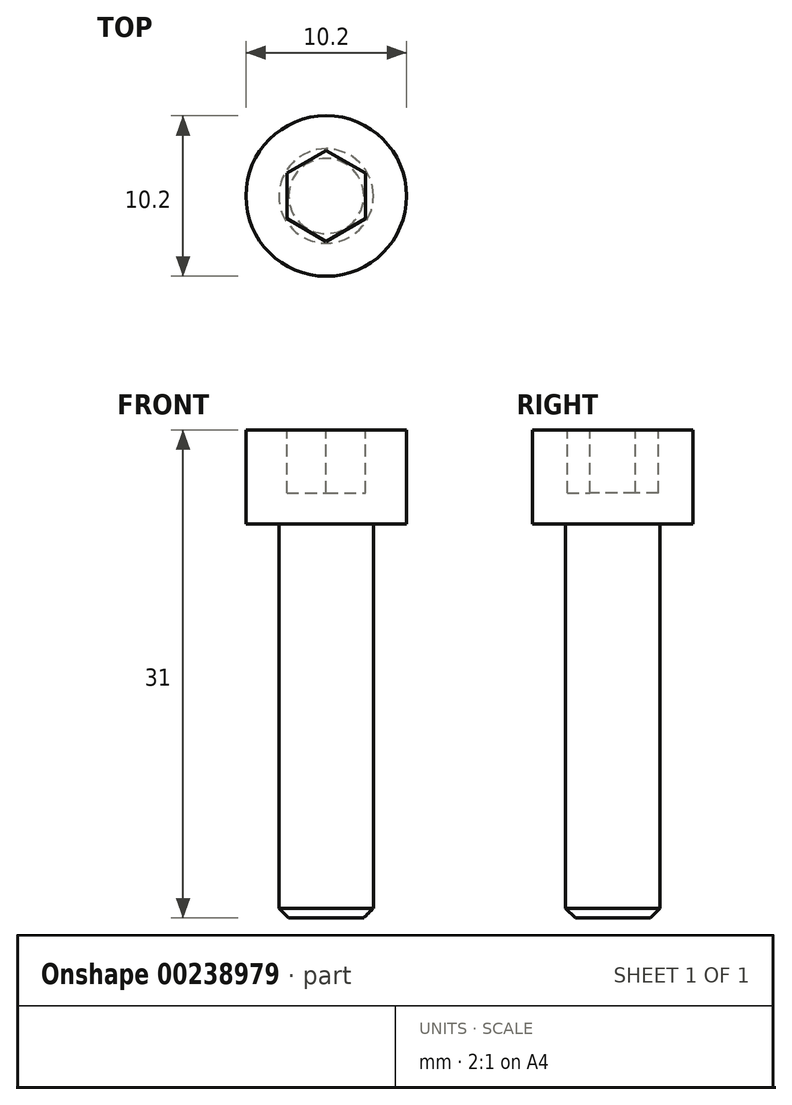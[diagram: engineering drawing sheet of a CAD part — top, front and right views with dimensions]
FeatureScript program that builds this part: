
annotation { "Feature Type Name" : "Feature", "Feature Type Description" : "" }
export const myFeature = defineFeature(function(context is Context, id is Id, definition is map)
    precondition{}
    {
        {
            var Q0;
            Q0=qCreatedBy(makeId("Front.planeOp"),FACE);
            var sketch = newSketch(context, id + "F0", { "sketchPlane" : qUnion([Q0])});
            skLineSegment(sketch, "E0", {"start": v(-5.1, 6) * mm, "end": v(-5.1, 0) * mm});
            skLineSegment(sketch, "E1", {"start": v(-5.1, 6) * mm, "end": v(0, 6) * mm});
            skLineSegment(sketch, "E2", {"start": v(-3, 0) * mm, "end": v(-3, -24.39) * mm});
            skCircle(sketch, "E3", {"center": v(0, 0) * mm, "radius": 2.38 * mm, "construction": true});
            skLineSegment(sketch, "E4", {"start": v(0, -25) * mm, "end": v(-2.38, -25) * mm});
            skLineSegment(sketch, "E5", {"start": v(-2.38, 0) * mm, "end": v(-2.38, -42.56) * mm, "construction": true});
            skLineSegment(sketch, "E6", {"start": v(-2.38, -25) * mm, "end": v(-3, -24.39) * mm});
            skLineSegment(sketch, "E7", {"start": v(-5.1, 0) * mm, "end": v(-3, 0) * mm});
            skLineSegment(sketch, "E8", {"start": v(0, 6) * mm, "end": v(0, -25) * mm});
            skSolve(sketch);
        }
        {
            var Q0;
            Q0=qSketchRegion(id+"F0",true);
            var Q1;
            Q1=sQuery(id+"F0.wireOp",EDGE,"E8");
            revolve(context, id + "F1", {"entities" : qUnion([Q0]), "axis" : qUnion([Q1]), "revolveType" : RevolveType.FULL});
        }
        {
            var Q0;
            Q0=makeQuery(id+"F1.opRevolve","SWEPT_FACE",FACE,{"disambiguationData":[OSD([sQuery(id+"F0.wireOp",EDGE,"E1")])]});
            cPlane(context, id + "F2", {"entities" : qUnion([Q0]), "cplaneType" : CPlaneType.OFFSET, "offset" : 0 * mm, "width" : 150 * mm, "height" : 150 * mm});
        }
        {
            var Q0;
            Q0=qCreatedBy(id+"F2.planeOp",FACE);
            var sketch = newSketch(context, id + "F3", { "sketchPlane" : qUnion([Q0])});
            skCircle(sketch, "E9.cCircle", {"center": v(0, 0) * mm, "radius": 2.5 * mm, "construction": true});
            skLineSegment(sketch, "E9.0", {"start": v(2.5, 1.44) * mm, "end": v(2.5, -1.44) * mm});
            skLineSegment(sketch, "E9.1", {"start": v(2.5, -1.44) * mm, "end": v(0, -2.89) * mm});
            skLineSegment(sketch, "E9.2", {"start": v(0, -2.89) * mm, "end": v(-2.5, -1.44) * mm});
            skLineSegment(sketch, "E9.3", {"start": v(-2.5, -1.44) * mm, "end": v(-2.5, 1.44) * mm});
            skLineSegment(sketch, "E9.4", {"start": v(-2.5, 1.44) * mm, "end": v(0, 2.89) * mm});
            skLineSegment(sketch, "E9.5", {"start": v(0, 2.89) * mm, "end": v(2.5, 1.44) * mm});
            skPoint(sketch, "E9.0.midPoint", {"position": v(2.5, 0) * mm});
            skSolve(sketch);
        }
        {
            var Q0;
            Q0=qSketchRegion(id+"F3",true);
            extrude(context, id + "F4", {"entities" : qUnion([Q0]), "operationType" : NewBodyOperationType.REMOVE, "oppositeDirection" : true, "depth" : 4 * mm, "hasSecondDirection" : true, "secondDirectionOppositeDirection" : false, "secondDirectionDepth" : 4 * mm});
        }
    });
